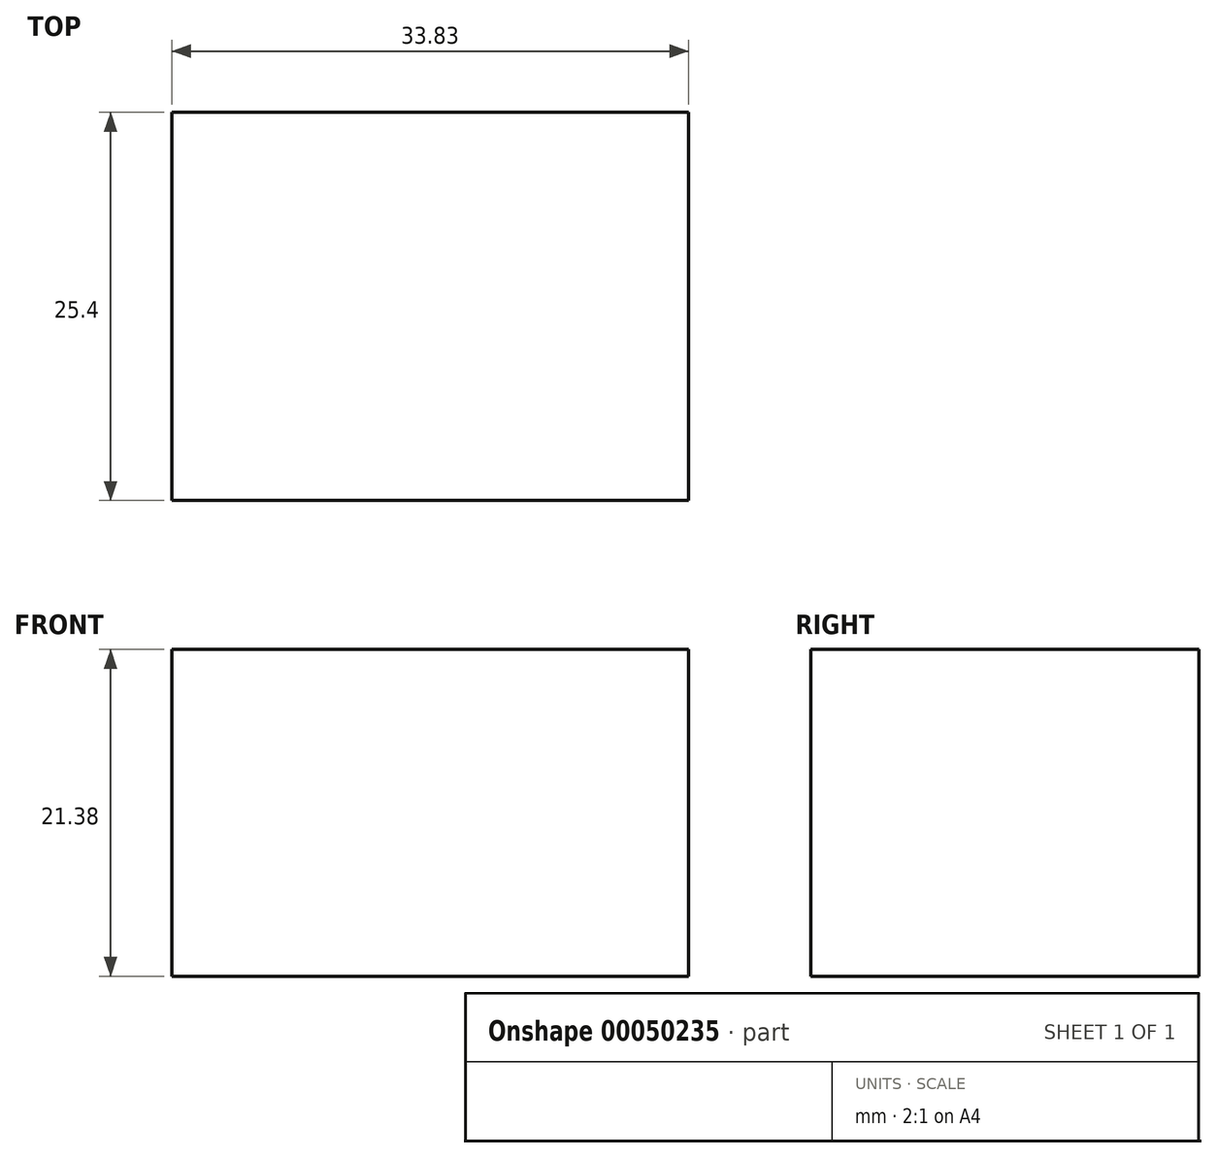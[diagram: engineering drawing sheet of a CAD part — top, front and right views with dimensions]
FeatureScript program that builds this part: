
annotation { "Feature Type Name" : "Feature", "Feature Type Description" : "" }
export const myFeature = defineFeature(function(context is Context, id is Id, definition is map)
    precondition{}
    {
        {
            var Q0;
            Q0=qCreatedBy(makeId("Front.planeOp"),FACE);
            var sketch = newSketch(context, id + "F0", { "sketchPlane" : qUnion([Q0])});
            skLineSegment(sketch, "E0.bottom", {"start": v(-16.53, 10.01) * mm, "end": v(17.3, 10.01) * mm});
            skLineSegment(sketch, "E0.top", {"start": v(-16.53, -11.37) * mm, "end": v(17.3, -11.37) * mm});
            skLineSegment(sketch, "E0.left", {"start": v(-16.53, 10.01) * mm, "end": v(-16.53, -11.37) * mm});
            skLineSegment(sketch, "E0.right", {"start": v(17.3, 10.01) * mm, "end": v(17.3, -11.37) * mm});
            skSolve(sketch);
        }
        {
            var Q0;
            Q0 = qSketchRegion(id + "F0", true);
            extrude(context, id + "F1", {"entities" : qUnion([Q0]), "depth" : 25.4 * mm});
        }
    });
